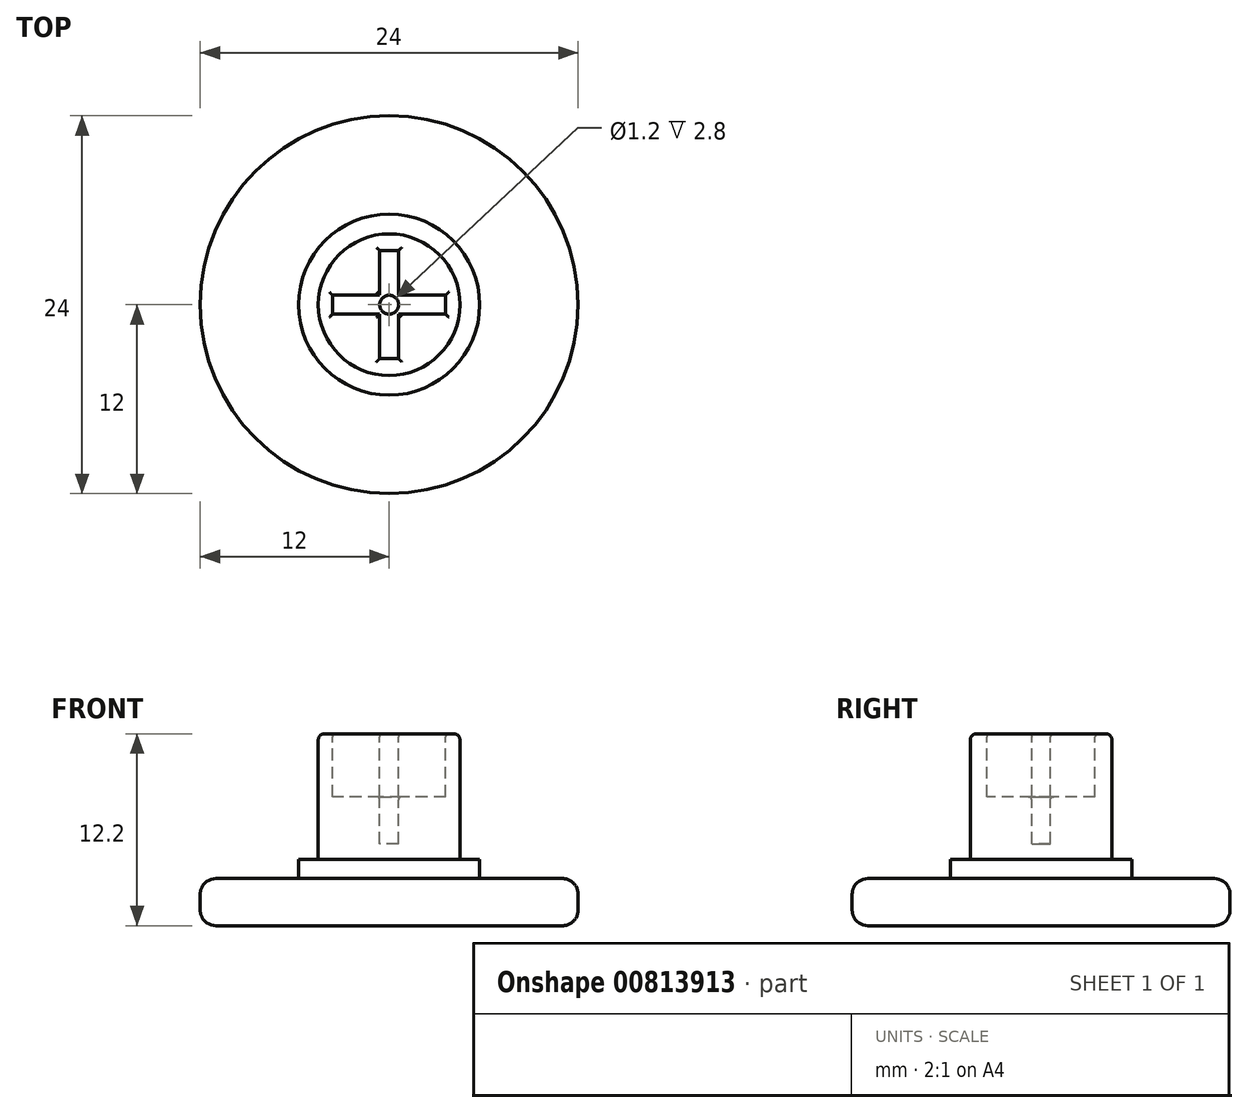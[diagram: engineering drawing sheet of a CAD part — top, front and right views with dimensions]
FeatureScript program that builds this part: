
annotation { "Feature Type Name" : "Feature", "Feature Type Description" : "" }
export const myFeature = defineFeature(function(context is Context, id is Id, definition is map)
    precondition{}
    {
        {
            var Q0;
            Q0=qCreatedBy(makeId("Top.planeOp"),FACE);
            var sketch = newSketch(context, id + "F0", { "sketchPlane" : qUnion([Q0])});
            skCircle(sketch, "E0", {"center": v(0, 0) * mm, "radius": 12 * mm});
            skSolve(sketch);
        }
        {
            var Q0;
            Q0=qSketchRegion(id+"F0",true);
            extrude(context, id + "F1", {"entities" : qUnion([Q0]), "depth" : 3 * mm});
        }
        {
            var Q0;
            Q0=makeQuery(id+"F1.opExtrude","CAP_FACE",FACE,{"disambiguationData":[OSD([sQuery(id+"F0.wireOp",EDGE,"E0")])],"isStart":false});
            var sketch = newSketch(context, id + "F2", { "sketchPlane" : qUnion([Q0])});
            skCircle(sketch, "E1", {"center": v(0, 0) * mm, "radius": 5.75 * mm});
            skSolve(sketch);
        }
        {
            var Q0;
            Q0=qSketchRegion(id+"F2",true);
            extrude(context, id + "F3", {"entities" : qUnion([Q0]), "operationType" : NewBodyOperationType.ADD, "depth" : 1.2 * mm});
        }
        {
            var Q0;
            Q0=makeQuery(id+"F3.opExtrude","CAP_FACE",FACE,{"disambiguationData":[OSD([sQuery(id+"F2.wireOp",EDGE,"E1")])],"isStart":false});
            var sketch = newSketch(context, id + "F4", { "sketchPlane" : qUnion([Q0])});
            skCircle(sketch, "E2", {"center": v(0, 0) * mm, "radius": 4.5 * mm});
            skSolve(sketch);
        }
        {
            var Q0;
            Q0=qSketchRegion(id+"F4",true);
            extrude(context, id + "F5", {"entities" : qUnion([Q0]), "operationType" : NewBodyOperationType.ADD, "depth" : 8 * mm, "offsetDistance" : 25 * mm});
        }
        {
            var Q0;
            Q0=makeQuery(id+"F5.opExtrude","CAP_FACE",FACE,{"disambiguationData":[OSD([sQuery(id+"F4.wireOp",EDGE,"E2")])],"isStart":false});
            var sketch = newSketch(context, id + "F6", { "sketchPlane" : qUnion([Q0])});
            skCircle(sketch, "E3", {"center": v(0, 0) * mm, "radius": 0.6 * mm});
            skSolve(sketch);
        }
        {
            var Q0;
            Q0=makeQuery(id+"F3.opExtrude","CAP_FACE",FACE,{"disambiguationData":[OSD([sQuery(id+"F2.wireOp",EDGE,"E1")])],"isStart":false});
            cPlane(context, id + "F7", {"entities" : qUnion([Q0]), "cplaneType" : CPlaneType.OFFSET, "offset" : 6 * mm, "width" : 152.4 * mm, "height" : 152.4 * mm});
        }
        {
            var Q0;
            Q0=qCreatedBy(id+"F7.planeOp",FACE);
            var sketch = newSketch(context, id + "F8", { "sketchPlane" : qUnion([Q0])});
            skCircle(sketch, "E4", {"center": v(0, 0) * mm, "radius": 1.8 * mm});
            skCircle(sketch, "E5", {"center": v(0, 0) * mm, "radius": 2 * mm});
            skSolve(sketch);
        }
        {
            var Q0;
            Q0=makeQuery(id+"F8.imprint","IMPRINT",FACE,{"disambiguationData":[TD([[makeQuery(id+"F8.imprint","IMPRINT",EDGE,{"derivedFrom":sQuery(id+"F8.wireOp",EDGE,"E4")}),-1.0]])]});
            extrude(context, id + "F9", {"entities" : qUnion([Q0]), "operationType" : NewBodyOperationType.ADD, "depth" : 0.4 * mm});
        }
        {
            var Q0;
            Q0=qSketchRegion(id+"F6",true);
            extrude(context, id + "F10", {"entities" : qUnion([Q0]), "operationType" : NewBodyOperationType.REMOVE, "oppositeDirection" : true, "depth" : 7 * mm});
        }
        {
            var Q0;
            Q0=makeQuery(id+"F5.opExtrude","CAP_FACE",FACE,{"disambiguationData":[OSD([sQuery(id+"F4.wireOp",EDGE,"E2")])],"isStart":false});
            var sketch = newSketch(context, id + "F11", { "sketchPlane" : qUnion([Q0])});
            skLineSegment(sketch, "E6.bottom", {"start": v(-0.6, 3.43) * mm, "end": v(0.6, 3.43) * mm});
            skLineSegment(sketch, "E6.top", {"start": v(-0.6, -3.43) * mm, "end": v(0.6, -3.43) * mm});
            skLineSegment(sketch, "E6.left", {"start": v(-0.6, 3.43) * mm, "end": v(-0.6, -3.43) * mm});
            skLineSegment(sketch, "E6.right", {"start": v(0.6, 3.43) * mm, "end": v(0.6, -3.43) * mm});
            skPoint(sketch, "E6.middle", {"position": v(0, 0) * mm});
            skLineSegment(sketch, "E7.bottom", {"start": v(3.6, 0.6) * mm, "end": v(-3.6, 0.6) * mm});
            skLineSegment(sketch, "E7.top", {"start": v(3.6, -0.6) * mm, "end": v(-3.6, -0.6) * mm});
            skLineSegment(sketch, "E7.left", {"start": v(3.6, 0.6) * mm, "end": v(3.6, -0.6) * mm});
            skLineSegment(sketch, "E7.right", {"start": v(-3.6, 0.6) * mm, "end": v(-3.6, -0.6) * mm});
            skSolve(sketch);
        }
        {
            var Q0;
            Q0=qSketchRegion(id+"F11",true);
            extrude(context, id + "F12", {"entities" : qUnion([Q0]), "operationType" : NewBodyOperationType.REMOVE, "oppositeDirection" : true, "depth" : 4 * mm});
        }
        {
            var Q0;
            {var subQ0=sQuery(id+"F4.wireOp",EDGE,"E2");Q0=makeQuery(id+"F12.boolean.opBoolean","SPLIT",EDGE,{"disambiguationData":[TD([makeQuery(id+"F12.opExtrude","SWEPT_FACE",FACE,{"disambiguationData":[OSD([sQuery(id+"F11.wireOp",EDGE,"E6.left")])]})])],"derivedFrom":makeQuery(id+"F5.opExtrude","CAP_EDGE",EDGE,{"disambiguationData":[OSD([subQ0])],"isStart":false})});}
            var Q1;
            {var subQ0=sQuery(id+"F4.wireOp",EDGE,"E2");Q1=makeQuery(id+"F12.boolean.opBoolean","SPLIT",EDGE,{"disambiguationData":[TD([makeQuery(id+"F12.opExtrude","SWEPT_FACE",FACE,{"disambiguationData":[OSD([sQuery(id+"F11.wireOp",EDGE,"E6.right")])]})])],"derivedFrom":makeQuery(id+"F5.opExtrude","CAP_EDGE",EDGE,{"disambiguationData":[OSD([subQ0])],"isStart":false})});}
            fillet(context, id + "F13", {"entities" : qUnion([Q0, Q1]), "radius" : .4 * mm, "tangentPropagation" : true, "allowEdgeOverflow" : false});
        }
        {
            var Q0;
            Q0=makeQuery(id+"F1.opExtrude","CAP_EDGE",EDGE,{"disambiguationData":[OSD([sQuery(id+"F0.wireOp",EDGE,"E0")])],"isStart":false});
            var Q1;
            Q1=makeQuery(id+"F1.opExtrude","CAP_EDGE",EDGE,{"disambiguationData":[OSD([sQuery(id+"F0.wireOp",EDGE,"E0")])],"isStart":true});
            fillet(context, id + "F14", {"entities" : qUnion([Q0, Q1]), "radius" : 1 * mm, "tangentPropagation" : true, "allowEdgeOverflow" : false});
        }
        {
            var Q0;
            {var subQ0=sQuery(id+"F4.wireOp",EDGE,"E2");var subQ1=sQuery(id+"F11.wireOp",EDGE,"E7.bottom");var subQ2=sQuery(id+"F11.wireOp",EDGE,"E6.left");var subQ3=makeQuery(id+"F11.imprint","INTERSECT",VERTEX,{"derivedFrom":[subQ2,subQ1]});Q0=makeQuery(id+"F12.boolean.opBoolean","SPLIT",FACE,{"disambiguationData":[TD([makeQuery(id+"F12.opExtrude","SWEPT_FACE",FACE,{"disambiguationData":[OSD([subQ2]),TDD([makeQuery(id+"F11.imprint","IMPRINT",EDGE,{"disambiguationData":[TD([[makeQuery(id+"F11.imprint","INTERSECT",VERTEX,{"derivedFrom":[sQuery(id+"F11.wireOp",EDGE,"E6.bottom"),subQ2]}),-1.0]])],"derivedFrom":subQ2}),makeQuery(id+"F11.imprint","IMPRINT",EDGE,{"disambiguationData":[TD([[subQ3,1.0]])],"derivedFrom":subQ2})])]})])],"derivedFrom":makeQuery(id+"F5.opExtrude","CAP_FACE",FACE,{"disambiguationData":[OSD([subQ0])],"isStart":false})});}
            var Q1;
            {var subQ0=sQuery(id+"F4.wireOp",EDGE,"E2");var subQ1=sQuery(id+"F11.wireOp",EDGE,"E7.bottom");var subQ2=sQuery(id+"F11.wireOp",EDGE,"E6.right");var subQ3=makeQuery(id+"F11.imprint","INTERSECT",VERTEX,{"derivedFrom":[subQ2,subQ1]});Q1=makeQuery(id+"F12.boolean.opBoolean","SPLIT",FACE,{"disambiguationData":[TD([makeQuery(id+"F12.opExtrude","SWEPT_FACE",FACE,{"disambiguationData":[OSD([subQ2]),TDD([makeQuery(id+"F11.imprint","IMPRINT",EDGE,{"disambiguationData":[TD([[makeQuery(id+"F11.imprint","INTERSECT",VERTEX,{"derivedFrom":[sQuery(id+"F11.wireOp",EDGE,"E6.bottom"),subQ2]}),-1.0]])],"derivedFrom":subQ2}),makeQuery(id+"F11.imprint","IMPRINT",EDGE,{"disambiguationData":[TD([[subQ3,1.0]])],"derivedFrom":subQ2})])]})])],"derivedFrom":makeQuery(id+"F5.opExtrude","CAP_FACE",FACE,{"disambiguationData":[OSD([subQ0])],"isStart":false})});}
            var Q2;
            {var subQ0=sQuery(id+"F4.wireOp",EDGE,"E2");var subQ1=sQuery(id+"F11.wireOp",EDGE,"E7.top");var subQ2=sQuery(id+"F11.wireOp",EDGE,"E6.right");var subQ3=makeQuery(id+"F11.imprint","INTERSECT",VERTEX,{"derivedFrom":[subQ2,subQ1]});Q2=makeQuery(id+"F12.boolean.opBoolean","SPLIT",FACE,{"disambiguationData":[TD([makeQuery(id+"F12.opExtrude","SWEPT_FACE",FACE,{"disambiguationData":[OSD([subQ2]),TDD([makeQuery(id+"F11.imprint","IMPRINT",EDGE,{"disambiguationData":[TD([[subQ3,-1.0]])],"derivedFrom":subQ2}),makeQuery(id+"F11.imprint","IMPRINT",EDGE,{"disambiguationData":[TD([[makeQuery(id+"F11.imprint","INTERSECT",VERTEX,{"derivedFrom":[sQuery(id+"F11.wireOp",EDGE,"E6.top"),subQ2]}),1.0]])],"derivedFrom":subQ2})])]})])],"derivedFrom":makeQuery(id+"F5.opExtrude","CAP_FACE",FACE,{"disambiguationData":[OSD([subQ0])],"isStart":false})});}
            var Q3;
            {var subQ0=sQuery(id+"F4.wireOp",EDGE,"E2");var subQ1=sQuery(id+"F11.wireOp",EDGE,"E6.left");var subQ4=sQuery(id+"F11.wireOp",EDGE,"E7.top");var subQ5=makeQuery(id+"F11.imprint","INTERSECT",VERTEX,{"derivedFrom":[subQ1,subQ4]});Q3=makeQuery(id+"F12.boolean.opBoolean","SPLIT",FACE,{"disambiguationData":[TD([makeQuery(id+"F12.opExtrude","SWEPT_FACE",FACE,{"disambiguationData":[OSD([subQ1]),TDD([makeQuery(id+"F11.imprint","IMPRINT",EDGE,{"disambiguationData":[TD([[subQ5,-1.0]])],"derivedFrom":subQ1}),makeQuery(id+"F11.imprint","IMPRINT",EDGE,{"disambiguationData":[TD([[makeQuery(id+"F11.imprint","INTERSECT",VERTEX,{"derivedFrom":[sQuery(id+"F11.wireOp",EDGE,"E6.top"),subQ1]}),1.0]])],"derivedFrom":subQ1})])]})])],"derivedFrom":makeQuery(id+"F5.opExtrude","CAP_FACE",FACE,{"disambiguationData":[OSD([subQ0])],"isStart":false})});}
            var Q4;
            Q4=makeQuery(id+"F12.boolean.opBoolean","INTERSECT",EDGE,{"derivedFrom":[makeQuery(id+"F10.boolean.opBoolean","COPY",FACE,{"derivedFrom":makeQuery(id+"F10.opExtrude","SWEPT_FACE",FACE,{"disambiguationData":[OSD([sQuery(id+"F6.wireOp",EDGE,"E3")])]})}),makeQuery(id+"F12.opExtrude","CAP_FACE",FACE,{"disambiguationData":[OSD([sQuery(id+"F11.wireOp",EDGE,"E6.bottom"),sQuery(id+"F11.wireOp",EDGE,"E6.top"),sQuery(id+"F11.wireOp",EDGE,"E6.left"),sQuery(id+"F11.wireOp",EDGE,"E6.right"),sQuery(id+"F11.wireOp",EDGE,"E7.bottom"),sQuery(id+"F11.wireOp",EDGE,"E7.top"),sQuery(id+"F11.wireOp",EDGE,"E7.left"),sQuery(id+"F11.wireOp",EDGE,"E7.right")])],"isStart":false})]});
            fillet(context, id + "F15", {"entities" : qUnion([Q0, Q1, Q2, Q3, Q4]), "radius" : 0.2 * mm, "tangentPropagation" : true, "allowEdgeOverflow" : false});
        }
    });
